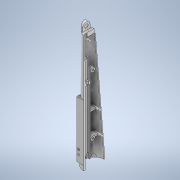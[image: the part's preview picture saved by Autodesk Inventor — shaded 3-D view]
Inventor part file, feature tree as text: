
AUTODESK INVENTOR PART (.ipt)
format: ipt  version: 2021 (Build 250183000, 183)  size: 1,121,792 bytes
history: native  units: mm
features: sketch x40, extrude x37, plane x17, fillet x7, hole x3, thread x3, loft x2, revolve x2, other x1
ambient origin geometry x8: Origin, YZ Plane, XZ Plane, XY Plane, X Axis, Y Axis, Z Axis, Center Point
bodies: Body1 (feature_tree)
feature tree (112):
  other  "Sólido1"
  plane  "Plano de trabajo1"
  plane  "Plano de trabajo2"
  plane  "Plano de trabajo4"
  plane  "Plano de trabajo5"
  plane  "Plano de trabajo6"
  sketch  "Boceto1"  dims[d1=250.0mm d2=0.0mm d3=-80.0mm d4=-110.0mm]
  sketch  "Boceto2"  dims[d5=-140.0mm d7=-0.0mm d8=2.0mm]
  sketch  "Boceto3"  dims[d9=140.0mm d10=250.0mm]
  sketch  "Boceto4"  dims[d11=24.0mm d22=0.0mm d23=90.0deg d24=0.0mm d25=90.0deg]
  sketch  "Boceto6"  dims[d44=45.0mm d49=29.11157mm]
  sketch  "Boceto7"  dims[d50=29.11157mm d53=29.11157mm]
  loft  "Solevación1"
  fillet  "Empalme2"  [1 undecoded]
  extrude  "Extrusión1"  TaperAngle=0.0deg  [1 undecoded]
  fillet  "Empalme5"  Radius=2.0mm
  plane  "Plano de trabajo7"
  extrude  "Extrusión2"  Depth=250.0mm
  plane  "Plano de trabajo8"
  plane  "Plano de trabajo9"
  loft  "Solevación9"
  plane  "Plano de trabajo10"
  extrude  "Extrusión3"  Depth=29.11157mm
  plane  "Plano de trabajo11"
  revolve  "Revolución1"  [1 undecoded]
  revolve  "Revolución2"  [1 undecoded]
  extrude  "Extrusión4"  Depth=32.5mm
  plane  "Plano de trabajo12"
  extrude  "Extrusión5"  Depth=44.747934mm
  plane  "Plano de trabajo13"
  plane  "Plano de trabajo14"
  extrude  "Extrusión6"  Depth=42.747934mm
  extrude  "Extrusión7"  Depth=42.747934mm
  extrude  "Extrusión8"  Depth=13.0mm
  extrude  "Extrusión11"  Depth=7.75mm
  extrude  "Extrusión9"  Depth=7.75mm
  extrude  "Extrusión10"  Depth=16.0mm
  extrude  "Extrusión12"  Depth=12.0mm
  sketch  "Boceto30"  dims[d160=-19.75mm d161=0.0mm]
  extrude  "Extrusión13"  Depth=7.75mm
  extrude  "Extrusión14"  Depth=7.75mm
  extrude  "Extrusión15"  TaperAngle=0.0deg  [1 undecoded]
  hole  "Agujero1"  [1 undecoded]
  thread  "Rosca1"  [1 undecoded]
  extrude  "Extrusión16"  Depth=2.0mm
  plane  "Plano de trabajo16"
  extrude  "Extrusión17"  TaperAngle=0.0deg  [1 undecoded]
  extrude  "Extrusión18"  TaperAngle=0.0deg  [1 undecoded]
  plane  "Plano de trabajo17"
  sketch  "Boceto46"  dims[d185=2.0mm d187=1.0mm]
  hole  "Agujero2"  [1 undecoded]
  hole  "Agujero3"  [1 undecoded]
  plane  "Plano de trabajo19"
  sketch  "Boceto50"  dims[d193=0.25mm d194=90.0deg d196=4.381635mm d197=0.0mm]
  extrude  "Extrusión22"  Depth=12.0mm
  extrude  "Extrusión23"  [1 undecoded]
  extrude  "Extrusión24"  Depth=0.75mm
  plane  "Plano de trabajo20"
  extrude  "Extrusión25"  Depth=1.0mm
  fillet  "Empalme6"  Radius=11.0mm
  fillet  "Empalme7"  Radius=17.453293mm
  sketch  "Boceto49"  dims[d191=2.0mm d192=0.25mm]
  extrude  "Extrusión29"  Depth=0.75mm
  extrude  "Extrusión30"  Depth=0.25mm
  sketch  "Boceto44"  dims[d181=0.75mm d182=0.25mm]
  sketch  "Boceto47"  dims[d189=3.0mm d190=2.0mm]
  extrude  "Extrusión26"  Depth=0.25mm
  extrude  "Extrusión27"  Depth=1.0mm
  extrude  "Extrusión28"  Depth=2.0mm
  sketch  "Boceto45"  dims[d183=1.0mm d184=0.25mm]
  extrude  "Extrusión31"  Depth=0.25mm
  extrude  "Extrusión32"  TaperAngle=90.0deg  [1 undecoded]
  fillet  "Empalme8"  Radius=4.381635mm
  extrude  "Extrusión33"  Depth=12.0mm
  extrude  "Extrusión34"  Depth=9.0mm
  thread  "Rosca2"  [1 undecoded]
  thread  "Rosca3"  [1 undecoded]
  fillet  "Empalme9"  Radius=201.65mm
  extrude  "Extrusión35"  Depth=0.5mm
  extrude  "Extrusión36"  [1 undecoded]
  sketch  "Boceto53"  dims[d205=0.0mm d206=0.5mm]
  extrude  "Agujero_tornillo_caja"  Depth=100.0mm TaperAngle=0.0deg
  extrude  "Extrusión39"  Depth=35.0mm TaperAngle=0.0deg
  extrude  "Test_section"  Depth=210.0mm TaperAngle=0.0deg
  extrude  "Agujero_cables"  Depth=2.0mm
  fillet  "Empalme10"  Radius=1.059493mm
  sketch  "Boceto9"  dims[d59=29.11157mm d61=29.11157mm]
  sketch  "Boceto10"  dims[d65=22.5mm d66=32.5mm]
  sketch  "Boceto15"  dims[d67=22.5mm d90=44.747934mm]
  sketch  "Boceto16"  dims[d91=42.747934mm d93=42.747934mm]
  sketch  "Boceto17"  dims[d96=0.0mm d97=90.0deg d98=0.0mm d99=90.0deg d100=0.0mm d101=90.0deg d102=0.0mm d103=90.0deg d112=42.747934mm]
  sketch  "Boceto18"  dims[d115=5.0mm d120=13.0mm]
  sketch  "Boceto19"  dims[d121=6.5mm d124=7.75mm]
  sketch  "Boceto20"  dims[d125=7.75mm d126=7.75mm]
  sketch  "Boceto21"  dims[d127=7.75mm d130=16.0mm]
  sketch  "Boceto22"  dims[d131=0.0mm d132=12.0mm]
  sketch  "Boceto24"  dims[d133=12.0mm d134=7.75mm]
  sketch  "Boceto25"  dims[d135=6.5mm d136=7.75mm]
  sketch  "Boceto26"  dims[d137=15.0mm d138=0.0mm]
  sketch  "Boceto27"  dims[d146=-8.5mm d147=30.0mm d148=2.0mm]
  sketch  "Boceto28"  dims[d149=25.12mm d150=2.0mm]
  sketch  "Boceto29"  dims[d151=10.357mm d156=0.0mm d157=90.0deg d158=0.0mm d159=90.0deg]
  sketch  "Boceto31"  dims[d163=0.0mm d164=2.0mm]
  sketch  "Boceto36"  dims[d165=15.0mm d166=4.0mm]
  sketch  "Boceto37"  dims[d167=30.0mm d168=12.0mm]
  sketch  "Boceto38"  dims[d169=0.0mm d170=-7.25mm]
  sketch  "Boceto39"  dims[d171=4.5mm d172=0.75mm]
  sketch  "Boceto40"  dims[d173=2.5mm d174=1.0mm d176=11.0mm d177=17.453293mm]
  sketch  "Boceto41"  dims[d179=2.939597mm d180=0.75mm]
  sketch  "Boceto51"  dims[d198=-48.35mm d199=12.0mm]
  sketch  "Boceto52"  dims[d200=20.0mm d201=9.0mm d202=9.0mm d203=2.0mm d204=201.65mm]
  sketch  "Boceto54"  dims[d207=0.25mm d208=-7.5mm d209=100.0mm d210=0.0mm d211=35.0mm d212=0.0mm d213=210.0mm d214=0.0mm d215=2.0mm d216=1.059493mm d217=6.5mm d218=1.059493mm d219=5.0mm d220=2.0mm d221=0.0mm d222=2.0mm d223=6.5mm d224=1.059493mm d225=5.0mm d226=4.85mm d227=2.0mm d228=0.0mm d229=6.0mm d230=10.0mm d231=3.0mm d232=11.0mm d233=10.5mm d235=30.0deg d236=4.75mm d237=0.0mm d238=-17.0mm d239=100.0mm d240=0.0mm d241=6.5mm d242=1.65mm d243=3.3mm d244=15.6mm d245=2.0mm d247=16.0mm d248=2.0mm d249=0.0mm d250=4.5mm d251=0.75mm d252=2.5mm d253=1.0mm d254=11.0mm d255=17.453293mm d256=2.939597mm d257=0.75mm d258=0.75mm d259=0.25mm d260=1.0mm d261=0.25mm d262=2.0mm d263=1.0mm d264=3.0mm d265=2.0mm d266=2.0mm d267=0.25mm d268=0.25mm d269=40.0mm d270=1.0mm d271=1.0mm d272=7.75mm d273=0.5mm d274=8.5mm d275=90.0deg d276=0.0mm d277=17.75mm d280=22.5mm d281=2.0mm d282=0.0mm d283=0.0mm d292=2.0mm d293=0.0mm d296=3.5mm d297=0.0mm d299=4.0mm d300=3.708mm d301=3.023mm d302=2.0mm d303=14.3117mm d304=16.0mm d305=0.0mm d306=16.0mm d307=0.0mm d314=6.0mm d315=19.2mm d316=6.0mm d317=19.2mm d318=13.0mm d320=6.0mm d321=19.2mm d322=13.0mm d323=6.0mm d324=19.2mm d325=13.0mm d326=7.0mm d332=10.0mm d333=0.0mm d335=-41.6mm d336=4.0mm d337=1.0mm d338=9.0mm d339=4.0mm d340=1.0mm d341=9.0mm d342=4.0mm d343=5.2mm d344=6.0mm d345=0.0mm d346=15.0mm d347=5.0mm d349=5.0mm d351=0.0mm d352=45.0mm d354=10.0mm d355=10.0mm d356=0.0mm d357=15.0mm d358=0.0mm d359=2.0mm d363=50.4125mm d376=14.059493mm d377=2.0mm d378=0.0mm d379=2.0mm d380=11.25mm d381=90.0mm d382=290.0mm d383=14.059493mm d384=100.825mm d390=30.940507mm d391=2.0mm d392=100.825mm d393=14.790546mm d394=2.0mm d395=3.0mm d396=4.0mm d397=4.0mm d398=4.0mm d399=4.0mm d400=8.128453mm d401=12.0mm d402=4.45mm d403=2.5mm d404=1.65mm d405=1.65mm d406=1.0mm d407=2.0mm d408=2.0mm d409=0.0mm d411=50.4125mm d412=4.0mm d418=13.059493mm d419=6.5mm d420=6.5mm d421=50.4125mm d422=126.03125mm d423=0.0mm d424=15.0mm d425=5.0mm d426=5.0mm d427=0.0mm d428=45.0mm d429=10.0mm d430=2.0mm d431=4.0mm d432=6.0mm d433=8.0mm d434=2.0mm d435=90.0deg d436=20.0mm d437=0.0mm d438=4.0mm d439=6.0mm d440=8.0mm d441=2.0mm d442=90.0deg d443=20.0mm d444=0.0mm d447=2.0mm d448=11.5mm d450=4.0mm d451=4.0mm d452=90.0mm d453=750.0mm d454=22.5mm d455=43.0mm d456=44.0mm d457=14.059493mm d458=11.25mm d461=22.5mm d462=43.0mm d463=7.059493mm d464=3.0mm d465=6.0mm d466=3.0mm d467=6.0mm d468=45.0mm d469=130.0mm d470=17.04mm d471=30.0mm d472=15.0mm d473=0.0mm d474=1.5mm d475=2.0mm d476=1.5mm d477=2.0mm d478=120.0mm d479=0.0mm d480=120.0mm d481=0.0mm d482=116.0mm d483=0.0mm d484=69.0mm d485=0.0mm d486=-1.5mm d487=65.395511mm d488=2.6mm d489=60.0deg d490=45.0deg d491=15.0mm d492=1.6mm d493=0.0mm d494=180.0mm d495=0.0mm d496=180.0mm d497=0.0mm d498=2.0mm d499=0.0mm d500=4.4mm d501=4.1mm d502=10.0mm d503=0.0mm d504=7.0mm d505=0.0mm d506=9.0mm d507=9.0mm d508=0.0mm d509=0.0mm d510=6.0mm d511=0.0mm d512=2.0mm d513=0.0mm d514=0.0mm d515=10.0mm d516=0.0mm d517=10.0mm d518=0.0mm d519=10.0mm d520=0.0mm d521=1.0mm d522=1.0mm d523=6.5mm d524=9.0mm d525=3.0mm d526=1.5mm d527=3.0mm d528=1.5mm d529=0.0mm d530=0.0mm d531=3.0mm d532=2.4mm d533=0.0mm d534=135.0mm d535=4.0mm d536=130.0mm d537=0.0mm d538=0.0mm d539=25.0mm d540=11.0mm d541=4.0mm d542=6.0mm d543=12.0mm d544=0.0mm d545=10.0mm d546=0.0mm d547=10.0mm d548=22.5mm d549=4.0mm d550=9.0mm d551=4.0mm d552=1.0mm d553=10.0mm d554=0.0mm d555=2.0mm d556=13.0mm d557=14.154386mm d558=14.654441mm d559=4.999945mm]
note: 16 required parameter values undecoded (feature->parameter linkage not recoverable at this tier; creation-order binding heuristic only, values carry confidence <= 0.55)